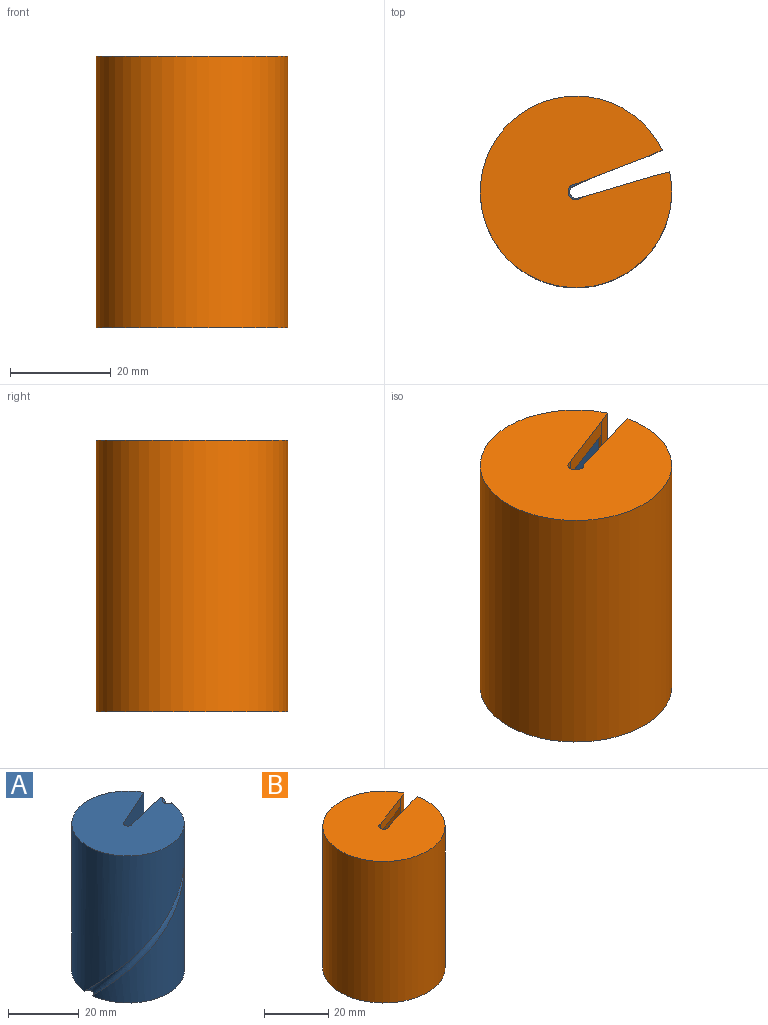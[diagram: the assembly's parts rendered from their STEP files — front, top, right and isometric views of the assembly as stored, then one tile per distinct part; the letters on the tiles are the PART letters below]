
ASSEMBLY  parts=2 mates=1
PART A: 8 faces, bbox 36.2x34x50.8 mm
  f0: plane 31.75x31.67mm, normal (0,0,1), area 723.2mm2, adj f2,f3,f4,f5,f6,f7
  f1: plane 31.75x31.67mm, normal (0,0,-1), area 723.2mm2, adj f2,f3,f4,f5,f6,f7
  f2: cylinder r=15.88mm len=50.8mm, axis (0,0,-1), area 3317.2mm2, adj f0,f1,f6,f7
  f3: cylinder r=1.27mm len=50.8mm, axis (0,0,-1), area 191.4mm2, adj f0,f1,f5,f6
  f4: cylinder r=15.88mm len=50.8mm, axis (0,0,-1), area 1318.5mm2, adj f0,f1,f5,f7
  f5: plane 50.8x15.35mm, normal (-0.24,0.97,0), area 803.9mm2, adj f0,f1,f3,f4
  f6: plane 50.8x14.46mm, normal (0.41,-0.91,0), area 803.9mm2, adj f0,f1,f2,f3
  f7: bspline ~50.8x36.19mm, area 295.1mm2, adj f0,f1,f2,f4
PART B: 12 faces, bbox 38.1x38.1x54 mm
  f0: cylinder r=15.88mm len=50.8mm, axis (0,0,1), area 3356mm2, adj f2,f4,f6,f11
  f1: cylinder r=19.05mm len=53.98mm, axis (0,0,-1), area 6212.5mm2, adj f2,f3,f4,f10
  f2: plane 38.1x38.1mm, normal (0,0,-1), area 337.9mm2, adj f0,f1,f3,f4,f5,f6
  f3: plane 53.98x3.08mm, normal (-0.24,0.97,0), area 171.5mm2, adj f1,f2,f5,f7,f10
  f4: plane 53.98x2.9mm, normal (0.41,-0.91,0), area 171.5mm2, adj f0,f1,f2,f9,f10
  f5: cylinder r=15.88mm len=50.8mm, axis (0,0,1), area 1357.3mm2, adj f2,f3,f6,f11
  f6: bspline ~50.8x32.2mm, area 272.3mm2, adj f0,f2,f5,f11
  f7: plane 14.35x4.26mm, normal (-0.28,0.96,0), area 47.5mm2, adj f3,f8,f10,f11
  f8: cylinder r=1.59mm len=3.18mm, axis (0,0,-1), area 20.2mm2, adj f7,f9,f10,f11
  f9: plane 14.23x5.44mm, normal (0.36,-0.93,0), area 48.4mm2, adj f4,f8,f10,f11
  f10: plane 38.1x38.1mm, normal (0,0,1), area 1068mm2, adj f1,f3,f4,f7,f8,f9
  f11: plane 31.75x31.68mm, normal (0,0,-1), area 730mm2, adj f0,f5,f6,f7,f8,f9
PLACE A t=(-2.44,45.05,0.82)mm
PLACE B t=(-2.44,45.05,0.82)mm fixed
MATE cylindrical A.f2 <-> B.f0  axis (0,0,-1) through (-2.44,45.05,26.22)mm
